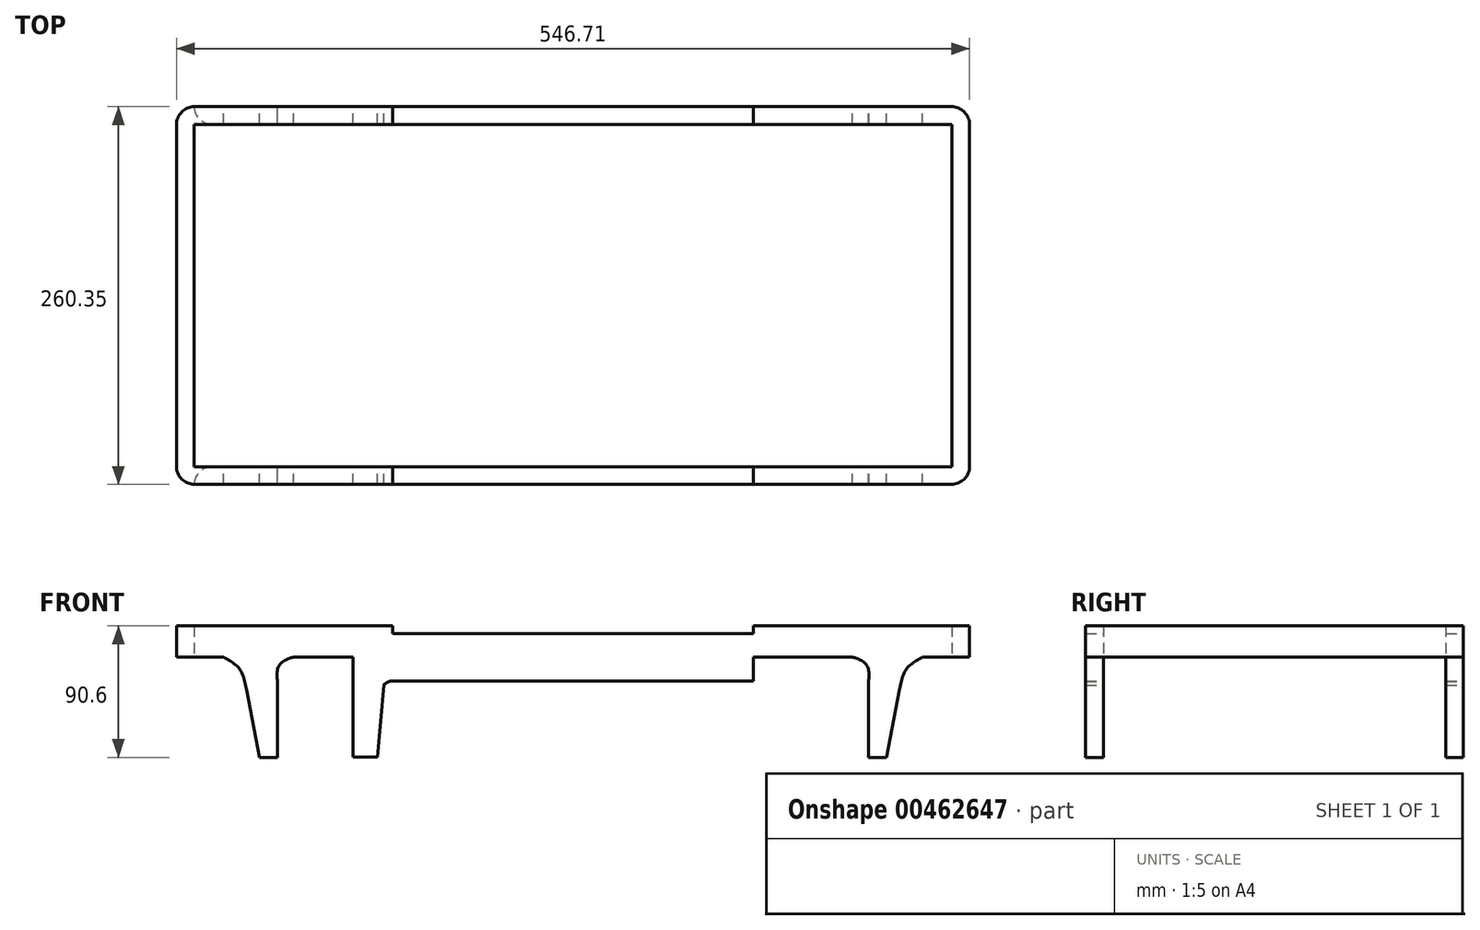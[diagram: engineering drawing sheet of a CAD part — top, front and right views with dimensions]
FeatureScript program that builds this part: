
annotation { "Feature Type Name" : "Feature", "Feature Type Description" : "" }
export const myFeature = defineFeature(function(context is Context, id is Id, definition is map)
    precondition{}
    {
        {
            var Q0;
            Q0=qCreatedBy(makeId("Front.planeOp"),FACE);
            var sketch = newSketch(context, id + "F0", { "sketchPlane" : qUnion([Q0])});
            skLineSegment(sketch, "E0.bottom", {"start": v(-132.87, 44.91) * mm, "end": v(-8.71, 44.91) * mm});
            skLineSegment(sketch, "E0.top", {"start": v(-132.87, 12.24) * mm, "end": v(-8.71, 12.24) * mm});
            skLineSegment(sketch, "E0.left", {"start": v(-132.87, 44.91) * mm, "end": v(-132.87, 12.24) * mm});
            skLineSegment(sketch, "E0.right", {"start": v(-8.71, 44.91) * mm, "end": v(-8.71, 12.24) * mm});
            skLineSegment(sketch, "E1.bottom", {"start": v(-269.88, 50.18) * mm, "end": v(-132.87, 50.18) * mm});
            skLineSegment(sketch, "E1.top", {"start": v(-269.88, 28.58) * mm, "end": v(-132.87, 28.58) * mm});
            skLineSegment(sketch, "E1.left", {"start": v(-269.88, 50.18) * mm, "end": v(-269.88, 28.58) * mm});
            skLineSegment(sketch, "E1.right", {"start": v(-132.87, 50.18) * mm, "end": v(-132.87, 28.58) * mm});
            skFitSpline(sketch, "E2", {"points": [v(-249.59, 28.58) * mm, v(-238.59, 20.6) * mm, v(-233.77, 6.17) * mm], "startDerivative": vector(25.88, -13.56) * mm, "endDerivative": vector(5.94, -31.09) * mm});
            skFitSpline(sketch, "E3", {"points": [v(-199.46, 28.58) * mm, v(-201.38, 28.58) * mm, v(-210.7, 23.74) * mm, v(-212.37, 11.88) * mm], "startDerivative": vector(-8.46, 1.35) * mm, "endDerivative": vector(2.85, -30.94) * mm});
            skLineSegment(sketch, "E4", {"start": v(-212.37, 11.88) * mm, "end": v(-212.37, -40.42) * mm});
            skLineSegment(sketch, "E5", {"start": v(-160.36, -40.12) * mm, "end": v(-160.36, 28.58) * mm});
            skArc(sketch, "E6", {"start": v(-132.87, 12.24) * mm, "mid": v(-136.33, 11.52) * mm, "end": v(-139.2, 9.48) * mm});
            skLineSegment(sketch, "E7", {"start": v(-139.2, 9.48) * mm, "end": v(-143.32, -40.12) * mm});
            skLineSegment(sketch, "E8", {"start": v(-233.77, 6.17) * mm, "end": v(-224.75, -40.42) * mm});
            skLineSegment(sketch, "E9", {"start": v(-224.75, -40.42) * mm, "end": v(-212.37, -40.42) * mm});
            skLineSegment(sketch, "E10", {"start": v(-160.36, -40.12) * mm, "end": v(-143.32, -40.12) * mm});
            skLineSegment(sketch, "E11", {"start": v(-8.71, 90.8) * mm, "end": v(-8.71, -84.57) * mm, "construction": true});
            skArc(sketch, "E12.MirrorCS", {"start": v(115.45, 12.24) * mm, "mid": v(118.9, 11.52) * mm, "end": v(121.78, 9.48) * mm});
            skFitSpline(sketch, "E13.MirrorCS", {"points": [v(182.03, 28.58) * mm, v(183.95, 28.58) * mm, v(193.27, 23.74) * mm, v(194.94, 11.88) * mm], "startDerivative": vector(8.46, 1.35) * mm, "endDerivative": vector(-2.85, -30.94) * mm});
            skFitSpline(sketch, "E14.MirrorCS", {"points": [v(232.16, 28.58) * mm, v(221.16, 20.6) * mm, v(216.35, 6.17) * mm], "startDerivative": vector(-25.88, -13.56) * mm, "endDerivative": vector(-5.94, -31.09) * mm});
            skLineSegment(sketch, "E15.MirrorCS", {"start": v(252.45, 28.58) * mm, "end": v(115.45, 28.58) * mm});
            skLineSegment(sketch, "E16.MirrorCS", {"start": v(252.45, 50.18) * mm, "end": v(252.45, 28.58) * mm});
            skLineSegment(sketch, "E17.MirrorCS", {"start": v(142.93, -40.12) * mm, "end": v(142.93, 28.58) * mm});
            skLineSegment(sketch, "E18.MirrorCS", {"start": v(207.33, -40.42) * mm, "end": v(194.94, -40.42) * mm});
            skLineSegment(sketch, "E19.MirrorCS", {"start": v(121.78, 9.48) * mm, "end": v(125.9, -40.12) * mm});
            skLineSegment(sketch, "E20.MirrorCS", {"start": v(115.45, 44.91) * mm, "end": v(-8.71, 44.91) * mm});
            skLineSegment(sketch, "E21.MirrorCS", {"start": v(115.45, 50.18) * mm, "end": v(115.45, 28.58) * mm});
            skLineSegment(sketch, "E22.MirrorCS", {"start": v(252.45, 50.18) * mm, "end": v(115.45, 50.18) * mm});
            skLineSegment(sketch, "E23.MirrorCS", {"start": v(194.94, 11.88) * mm, "end": v(194.94, -40.42) * mm});
            skLineSegment(sketch, "E24.MirrorCS", {"start": v(142.93, -40.12) * mm, "end": v(125.9, -40.12) * mm});
            skLineSegment(sketch, "E25.MirrorCS", {"start": v(115.45, 12.24) * mm, "end": v(-8.71, 12.24) * mm});
            skLineSegment(sketch, "E26.MirrorCS", {"start": v(216.35, 6.17) * mm, "end": v(207.33, -40.42) * mm});
            skLineSegment(sketch, "E27.MirrorCS", {"start": v(115.45, 44.91) * mm, "end": v(115.45, 12.24) * mm});
            skLineSegment(sketch, "E28", {"start": v(-186.78, 28.58) * mm, "end": v(-186.78, -48.75) * mm, "construction": true});
            skLineSegment(sketch, "E29", {"start": v(168.82, 28.58) * mm, "end": v(168.82, -46.74) * mm, "construction": true});
            skSolve(sketch);
        }
        {
            var Q0;
            {var subQ3=sQuery(id+"F0.wireOp",EDGE,"E20.MirrorCS");Q0=makeQuery(id+"F0.imprint","IMPRINT",FACE,{"disambiguationData":[TD([[makeQuery(id+"F0.imprint","IMPRINT",EDGE,{"derivedFrom":subQ3}),1.0]])]});}
            var Q1;
            {var subQ4=sQuery(id+"F0.wireOp",EDGE,"E2");Q1=makeQuery(id+"F0.imprint","IMPRINT",FACE,{"disambiguationData":[TD([[makeQuery(id+"F0.imprint","IMPRINT",EDGE,{"derivedFrom":subQ4}),1.0]])]});}
            var Q2;
            {var subQ1=sQuery(id+"F0.wireOp",EDGE,"E14.MirrorCS");Q2=makeQuery(id+"F0.imprint","IMPRINT",FACE,{"disambiguationData":[TD([[makeQuery(id+"F0.imprint","IMPRINT",EDGE,{"derivedFrom":subQ1}),-1.0]])]});}
            var Q3;
            {var subQ2=sQuery(id+"F0.wireOp",EDGE,"E0.left");Q3=makeQuery(id+"F0.imprint","IMPRINT",FACE,{"disambiguationData":[TD([[makeQuery(id+"F0.imprint","IMPRINT",EDGE,{"derivedFrom":subQ2}),-1.0]])]});}
            var Q4;
            {var subQ4=sQuery(id+"F0.wireOp",EDGE,"E12.MirrorCS");Q4=makeQuery(id+"F0.imprint","IMPRINT",FACE,{"disambiguationData":[TD([[makeQuery(id+"F0.imprint","IMPRINT",EDGE,{"derivedFrom":subQ4}),1.0]])]});}
            var Q5;
            {var subQ6=sQuery(id+"F0.wireOp",EDGE,"E16.MirrorCS");Q5=makeQuery(id+"F0.imprint","IMPRINT",FACE,{"disambiguationData":[TD([[makeQuery(id+"F0.imprint","IMPRINT",EDGE,{"derivedFrom":subQ6}),-1.0]])]});}
            var Q6;
            {var subQ2=sQuery(id+"F0.wireOp",EDGE,"E0.bottom");Q6=makeQuery(id+"F0.imprint","IMPRINT",FACE,{"disambiguationData":[TD([[makeQuery(id+"F0.imprint","IMPRINT",EDGE,{"derivedFrom":subQ2}),-1.0]])]});}
            var Q7;
            {var subQ7=sQuery(id+"F0.wireOp",EDGE,"E1.bottom");Q7=makeQuery(id+"F0.imprint","IMPRINT",FACE,{"disambiguationData":[TD([[makeQuery(id+"F0.imprint","IMPRINT",EDGE,{"derivedFrom":subQ7}),-1.0]])]});}
            var Q8;
            {var subQ0=sQuery(id+"F0.wireOp",EDGE,"E15.MirrorCS");var subQ1=sQuery(id+"F0.wireOp",EDGE,"E13.MirrorCS");var subQ2=makeQuery(id+"F0.imprint","INTERSECT",VERTEX,{"disambiguationData":[OD(0.0)],"derivedFrom":[subQ1,subQ0]});Q8=makeQuery(id+"F0.imprint","IMPRINT",FACE,{"disambiguationData":[TD([[makeQuery(id+"F0.imprint","IMPRINT",EDGE,{"disambiguationData":[TD([[subQ2,-1.0]])],"derivedFrom":subQ1}),-1.0]])]});}
            var Q9;
            {var subQ0=sQuery(id+"F0.wireOp",EDGE,"E3");var subQ1=sQuery(id+"F0.wireOp",EDGE,"E1.top");var subQ2=makeQuery(id+"F0.imprint","INTERSECT",VERTEX,{"disambiguationData":[OD(0.0)],"derivedFrom":[subQ1,subQ0]});Q9=makeQuery(id+"F0.imprint","IMPRINT",FACE,{"disambiguationData":[TD([[makeQuery(id+"F0.imprint","IMPRINT",EDGE,{"disambiguationData":[TD([[subQ2,1.0]])],"derivedFrom":subQ1}),1.0]])]});}
            extrude(context, id + "F1", {"entities" : qUnion([Q0, Q1, Q2, Q3, Q4, Q5, Q6, Q7, Q8, Q9]), "offsetDistance" : 25.4 * mm, "depth" : 12.2 * mm});
        }
        {
            var Q0;
            Q0=makeQuery(id+"F1.opExtrude","SWEPT_BODY",BODY,{"disambiguationData":[OSD([sQuery(id+"F0.wireOp",EDGE,"E0.bottom"),sQuery(id+"F0.wireOp",EDGE,"E0.top"),sQuery(id+"F0.wireOp",EDGE,"E1.bottom"),sQuery(id+"F0.wireOp",EDGE,"E1.top"),sQuery(id+"F0.wireOp",EDGE,"E1.left"),sQuery(id+"F0.wireOp",EDGE,"E1.right"),sQuery(id+"F0.wireOp",EDGE,"E2"),sQuery(id+"F0.wireOp",EDGE,"E3"),sQuery(id+"F0.wireOp",EDGE,"E4"),sQuery(id+"F0.wireOp",EDGE,"E5"),sQuery(id+"F0.wireOp",EDGE,"E6"),sQuery(id+"F0.wireOp",EDGE,"E7"),sQuery(id+"F0.wireOp",EDGE,"E8"),sQuery(id+"F0.wireOp",EDGE,"E9"),sQuery(id+"F0.wireOp",EDGE,"E10"),sQuery(id+"F0.wireOp",EDGE,"E12.MirrorCS"),sQuery(id+"F0.wireOp",EDGE,"E13.MirrorCS"),sQuery(id+"F0.wireOp",EDGE,"E14.MirrorCS"),sQuery(id+"F0.wireOp",EDGE,"E15.MirrorCS"),sQuery(id+"F0.wireOp",EDGE,"E16.MirrorCS"),sQuery(id+"F0.wireOp",EDGE,"E17.MirrorCS"),sQuery(id+"F0.wireOp",EDGE,"E18.MirrorCS"),sQuery(id+"F0.wireOp",EDGE,"E19.MirrorCS"),sQuery(id+"F0.wireOp",EDGE,"E20.MirrorCS"),sQuery(id+"F0.wireOp",EDGE,"E21.MirrorCS"),sQuery(id+"F0.wireOp",EDGE,"E22.MirrorCS"),sQuery(id+"F0.wireOp",EDGE,"E23.MirrorCS"),sQuery(id+"F0.wireOp",EDGE,"E24.MirrorCS"),sQuery(id+"F0.wireOp",EDGE,"E25.MirrorCS"),sQuery(id+"F0.wireOp",EDGE,"E26.MirrorCS")])]});
            transform(context, id + "F2", {"entities" : qUnion([Q0]), "transformType" : TransformType.TRANSLATION_3D, "dx" : 0 * mm, "dy" : -248.16 * mm, "dz" : 0 * mm, "makeCopy" : true});
        }
        {
            var Q0;
            Q0=makeQuery(id+"F2.opPattern","COPY",FACE,{"derivedFrom":makeQuery(id+"F1.opExtrude","SWEPT_FACE",FACE,{"disambiguationData":[OSD([sQuery(id+"F0.wireOp",EDGE,"E16.MirrorCS")])]}),"instanceName":"1"});
            var sketch = newSketch(context, id + "F3", { "sketchPlane" : qUnion([Q0])});
            skPoint(sketch, "E30.oppositeSnap0", {"position": v(-254.25, 28.58) * mm});
            skLineSegment(sketch, "E30.bottom", {"start": v(-260.35, 50.18) * mm, "end": v(0, 50.18) * mm});
            skLineSegment(sketch, "E30.top", {"start": v(-260.35, 28.58) * mm, "end": v(0, 28.58) * mm});
            skLineSegment(sketch, "E30.left", {"start": v(-260.35, 50.18) * mm, "end": v(-260.35, 28.58) * mm});
            skLineSegment(sketch, "E30.right", {"start": v(0, 50.18) * mm, "end": v(0, 28.58) * mm});
            skSolve(sketch);
        }
        {
            var Q0;
            Q0 = qSketchRegion(id + "F3", true);
            extrude(context, id + "F4", {"entities" : qUnion([Q0]), "operationType" : NewBodyOperationType.ADD, "depth" : 12.2 * mm, "offsetDistance" : 25.4 * mm});
        }
        {
            var Q0;
            Q0=makeQuery(id+"F1.opExtrude","SWEPT_FACE",FACE,{"disambiguationData":[OSD([sQuery(id+"F0.wireOp",EDGE,"E1.left")])]});
            var sketch = newSketch(context, id + "F5", { "sketchPlane" : qUnion([Q0])});
            skLineSegment(sketch, "E31.bottom", {"start": v(0, 50.18) * mm, "end": v(260.35, 50.18) * mm});
            skLineSegment(sketch, "E31.top", {"start": v(0, 28.6) * mm, "end": v(260.35, 28.6) * mm});
            skLineSegment(sketch, "E31.left", {"start": v(0, 50.18) * mm, "end": v(0, 28.6) * mm});
            skLineSegment(sketch, "E31.right", {"start": v(260.35, 50.18) * mm, "end": v(260.35, 28.6) * mm});
            skSolve(sketch);
        }
        {
            var Q0;
            Q0 = qSketchRegion(id + "F5", true);
            extrude(context, id + "F6", {"entities" : qUnion([Q0]), "operationType" : NewBodyOperationType.ADD, "depth" : 12.2 * mm, "offsetDistance" : 25.4 * mm});
        }
        {
            var Q0;
            Q0=makeQuery(id+"F4.opExtrude","CAP_EDGE",EDGE,{"disambiguationData":[OSD([sQuery(id+"F3.wireOp",EDGE,"E30.left")])],"isStart":false});
            var Q1;
            Q1=makeQuery(id+"F4.opExtrude","CAP_EDGE",EDGE,{"disambiguationData":[OSD([sQuery(id+"F3.wireOp",EDGE,"E30.right")])],"isStart":false});
            var Q2;
            Q2=makeQuery(id+"F6.opExtrude","CAP_EDGE",EDGE,{"disambiguationData":[OSD([sQuery(id+"F5.wireOp",EDGE,"E31.left")])],"isStart":false});
            var Q3;
            Q3=makeQuery(id+"F6.opExtrude","CAP_EDGE",EDGE,{"disambiguationData":[OSD([sQuery(id+"F5.wireOp",EDGE,"E31.right")])],"isStart":false});
            var Q4;
            Q4=makeQuery(id+"F1.opExtrude","CAP_EDGE",EDGE,{"disambiguationData":[OSD([sQuery(id+"F0.wireOp",EDGE,"E16.MirrorCS")])],"isStart":false});
            var Q5;
            Q5=makeQuery(id+"F2.opPattern","COPY",EDGE,{"derivedFrom":makeQuery(id+"F1.opExtrude","CAP_EDGE",EDGE,{"disambiguationData":[OSD([sQuery(id+"F0.wireOp",EDGE,"E16.MirrorCS")])],"isStart":true}),"instanceName":"1"});
            var Q6;
            {var subQ0=sQuery(id+"F0.wireOp",EDGE,"E1.left");Q6=makeQuery(id+"F6.boolean.opBoolean","SPLIT",EDGE,{"disambiguationData":[topologyDisambiguationEdgeConnected([makeQuery(id+"F6.opExtrude","CAP_FACE",FACE,{"disambiguationData":[OSD([sQuery(id+"F5.wireOp",EDGE,"E31.bottom"),sQuery(id+"F5.wireOp",EDGE,"E31.top"),sQuery(id+"F5.wireOp",EDGE,"E31.left"),sQuery(id+"F5.wireOp",EDGE,"E31.right")])],"isStart":true})])],"derivedFrom":makeQuery(id+"F2.opPattern","COPY",EDGE,{"derivedFrom":makeQuery(id+"F1.opExtrude","CAP_EDGE",EDGE,{"disambiguationData":[OSD([subQ0])],"isStart":true}),"instanceName":"1"})});}
            var Q7;
            {var subQ0=sQuery(id+"F0.wireOp",EDGE,"E1.left");Q7=makeQuery(id+"F6.boolean.opBoolean","SPLIT",EDGE,{"disambiguationData":[topologyDisambiguationEdgeConnected([makeQuery(id+"F6.opExtrude","CAP_FACE",FACE,{"disambiguationData":[OSD([sQuery(id+"F5.wireOp",EDGE,"E31.bottom"),sQuery(id+"F5.wireOp",EDGE,"E31.top"),sQuery(id+"F5.wireOp",EDGE,"E31.left"),sQuery(id+"F5.wireOp",EDGE,"E31.right")])],"isStart":true})])],"derivedFrom":makeQuery(id+"F1.opExtrude","CAP_EDGE",EDGE,{"disambiguationData":[OSD([subQ0])],"isStart":false})});}
            fillet(context, id + "F7", {"entities" : qUnion([Q0, Q1, Q2, Q3, Q4, Q5, Q6, Q7]), "tangentPropagation" : true, "radius" : 12.7 * mm, "defaultsChanged" : false, "vertexSettings" : [], "allowEdgeOverflow" : false});
        }
    });
